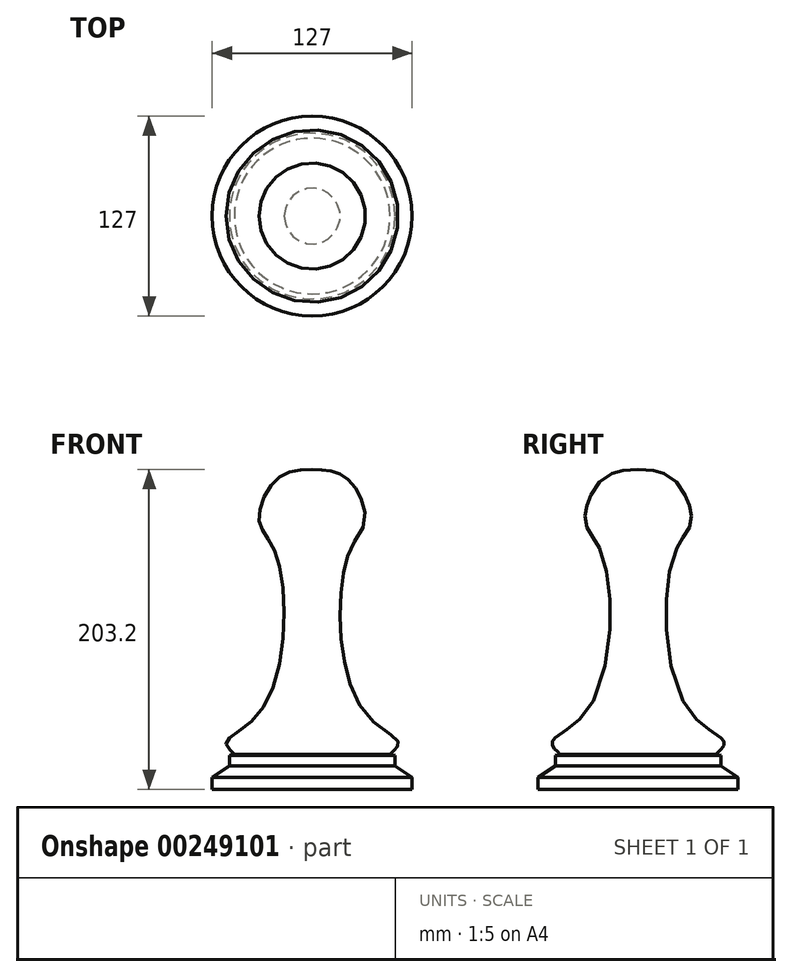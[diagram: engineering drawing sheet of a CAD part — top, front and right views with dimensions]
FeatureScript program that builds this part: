
annotation { "Feature Type Name" : "Feature", "Feature Type Description" : "" }
export const myFeature = defineFeature(function(context is Context, id is Id, definition is map)
    precondition{}
    {
        {
            var Q0;
            Q0=qCreatedBy(makeId("Front.planeOp"),FACE);
            var sketch = newSketch(context, id + "F0", { "sketchPlane" : qUnion([Q0])});
            skLineSegment(sketch, "E0", {"start": v(0, -120.05) * mm, "end": v(0, 123.26) * mm, "construction": true});
            skFitSpline(sketch, "E1", {"points": [v(0, 117.7) * mm, v(-22.25, 111.84) * mm, v(-33.67, 85.2) * mm, v(-22.59, 63.02) * mm, v(-31.83, -34.76) * mm, v(-54.75, -56.51) * mm, v(-49.45, -63.25) * mm, v(-49.15, -63.83) * mm], "startDerivative": vector(-174.15, -6.04) * mm, "endDerivative": vector(17.74, -18.18) * mm});
            skLineSegment(sketch, "E2", {"start": v(-49.15, -63.83) * mm, "end": v(-52.58, -63.83) * mm, "construction": true});
            skLineSegment(sketch, "E3", {"start": v(-63.5, -77.7) * mm, "end": v(-63.5, -85.5) * mm, "construction": true});
            skLineSegment(sketch, "E4", {"start": v(-63.5, -85.5) * mm, "end": v(0, -85.5) * mm});
            skLineSegment(sketch, "E5", {"start": v(0, -85.5) * mm, "end": v(0, 117.7) * mm});
            skLineSegment(sketch, "E6", {"start": v(-63.5, -85.5) * mm, "end": v(-63.5, -77.7) * mm});
            skLineSegment(sketch, "E7", {"start": v(-63.5, -77.7) * mm, "end": v(-52.58, -70.57) * mm});
            skLineSegment(sketch, "E8", {"start": v(-52.58, -70.57) * mm, "end": v(-52.58, -63.83) * mm});
            skLineSegment(sketch, "E9", {"start": v(-49.45, -63.25) * mm, "end": v(-52.58, -63.83) * mm});
            skSolve(sketch);
        }
        {
            var Q0;
            Q0=makeQuery(id+"F0.imprint","IMPRINT",FACE,{"disambiguationData":[TD([[makeQuery(id+"F0.imprint","IMPRINT",EDGE,{"derivedFrom":sQuery(id+"F0.wireOp",EDGE,"E4")}),1.0]])]});
            var Q1;
            Q1=sQuery(id+"F0.wireOp",EDGE,"E0");
            revolve(context, id + "F1", {"entities" : qUnion([Q0]), "axis" : qUnion([Q1]), "revolveType" : RevolveType.FULL});
        }
    });
